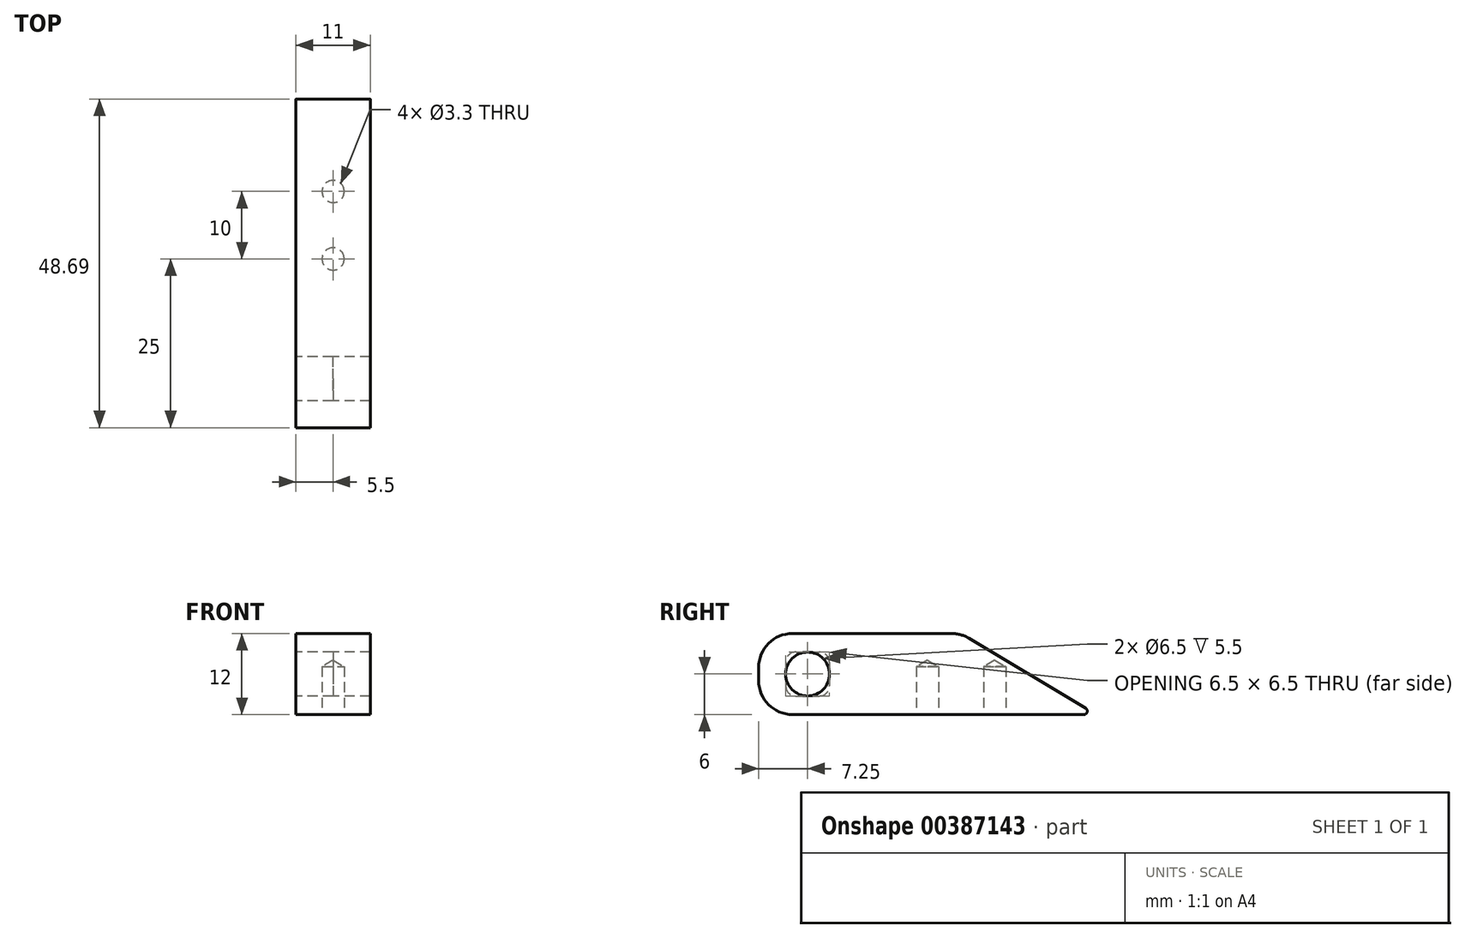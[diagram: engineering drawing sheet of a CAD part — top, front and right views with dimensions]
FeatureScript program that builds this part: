
annotation { "Feature Type Name" : "Feature", "Feature Type Description" : "" }
export const myFeature = defineFeature(function(context is Context, id is Id, definition is map)
    precondition{}
    {
        {
            var Q0;
            Q0=qCreatedBy(makeId("Front.planeOp"),FACE);
            var sketch = newSketch(context, id + "F0", { "sketchPlane" : qUnion([Q0])});
            skLineSegment(sketch, "E0.bottom", {"start": v(5.5, 6) * mm, "end": v(-5.5, 6) * mm});
            skLineSegment(sketch, "E0.top", {"start": v(5.5, -6) * mm, "end": v(-5.5, -6) * mm});
            skLineSegment(sketch, "E0.left", {"start": v(5.5, 6) * mm, "end": v(5.5, -6) * mm});
            skLineSegment(sketch, "E0.right", {"start": v(-5.5, 6) * mm, "end": v(-5.5, -6) * mm});
            skPoint(sketch, "E0.middle", {"position": v(0, 0) * mm});
            skSolve(sketch);
        }
        {
            var Q0;
            Q0 = qSketchRegion(id + "F0", true);
            extrude(context, id + "F1", {"entities" : qUnion([Q0]), "endBound" : BoundingType.SYMMETRIC, "depth" : 50 * mm});
        }
        {
            var Q0;
            Q0=makeQuery(id+"F1.opExtrude","SWEPT_FACE",FACE,{"disambiguationData":[OSD([sQuery(id+"F0.wireOp",EDGE,"E0.right")])]});
            var sketch = newSketch(context, id + "F2", { "sketchPlane" : qUnion([Q0])});
            skLineSegment(sketch, "E1.bottom", {"start": v(21, 3.25) * mm, "end": v(14.5, 3.25) * mm});
            skLineSegment(sketch, "E1.top", {"start": v(21, -3.25) * mm, "end": v(14.5, -3.25) * mm});
            skLineSegment(sketch, "E1.left", {"start": v(21, 3.25) * mm, "end": v(21, -3.25) * mm});
            skLineSegment(sketch, "E1.right", {"start": v(14.5, 3.25) * mm, "end": v(14.5, -3.25) * mm});
            skPoint(sketch, "E2.centerSnap0", {"position": v(21, 0) * mm});
            skPoint(sketch, "E2.centerSnap1", {"position": v(17.75, 3.25) * mm});
            skSolve(sketch);
        }
        {
            var Q0;
            Q0 = qSketchRegion(id + "F2", true);
            extrude(context, id + "F3", {"entities" : qUnion([Q0]), "operationType" : NewBodyOperationType.REMOVE, "oppositeDirection" : true, "depth" : 5.5 * mm});
        }
        {
            var Q0;
            Q0=makeQuery(id+"F3.boolean.opBoolean","COPY",FACE,{"derivedFrom":makeQuery(id+"F3.opExtrude","CAP_FACE",FACE,{"disambiguationData":[OSD([sQuery(id+"F2.wireOp",EDGE,"E1.bottom"),sQuery(id+"F2.wireOp",EDGE,"E1.top"),sQuery(id+"F2.wireOp",EDGE,"E1.left"),sQuery(id+"F2.wireOp",EDGE,"E1.right")])],"isStart":false})});
            var sketch = newSketch(context, id + "F4", { "sketchPlane" : qUnion([Q0])});
            skCircle(sketch, "E3", {"center": v(17.75, 0) * mm, "radius": 3.25 * mm});
            skPoint(sketch, "E3.centerSnap0", {"position": v(21, 0) * mm});
            skPoint(sketch, "E3.centerSnap1", {"position": v(17.75, 3.25) * mm});
            skSolve(sketch);
        }
        {
            var Q0;
            Q0 = qSketchRegion(id + "F4", true);
            extrude(context, id + "F5", {"entities" : qUnion([Q0]), "operationType" : NewBodyOperationType.REMOVE, "oppositeDirection" : true, "depth" : 25 * mm});
        }
        {
            var Q0;
            Q0=makeQuery(id+"F3.boolean.opBoolean","COPY",EDGE,{"derivedFrom":makeQuery(id+"F3.opExtrude","SWEPT_EDGE",EDGE,{"disambiguationData":[OSD([sQuery(id+"F2.wireOp",EDGE,"E1.bottom"),sQuery(id+"F2.wireOp",EDGE,"E1.right")])]})});
            var Q1;
            Q1=makeQuery(id+"F3.boolean.opBoolean","COPY",EDGE,{"derivedFrom":makeQuery(id+"F3.opExtrude","SWEPT_EDGE",EDGE,{"disambiguationData":[OSD([sQuery(id+"F2.wireOp",EDGE,"E1.bottom"),sQuery(id+"F2.wireOp",EDGE,"E1.left")])]})});
            var Q2;
            Q2=makeQuery(id+"F3.boolean.opBoolean","COPY",EDGE,{"derivedFrom":makeQuery(id+"F3.opExtrude","SWEPT_EDGE",EDGE,{"disambiguationData":[OSD([sQuery(id+"F2.wireOp",EDGE,"E1.top"),sQuery(id+"F2.wireOp",EDGE,"E1.left")])]})});
            var Q3;
            Q3=makeQuery(id+"F3.boolean.opBoolean","COPY",EDGE,{"derivedFrom":makeQuery(id+"F3.opExtrude","SWEPT_EDGE",EDGE,{"disambiguationData":[OSD([sQuery(id+"F2.wireOp",EDGE,"E1.top"),sQuery(id+"F2.wireOp",EDGE,"E1.right")])]})});
            fillet(context, id + "F6", {"entities" : qUnion([Q0, Q1, Q2, Q3]), "radius" : 1.5 * mm, "tangentPropagation" : true, "allowEdgeOverflow" : false});
        }
        {
            var Q0;
            Q0=makeQuery(id+"F1.opExtrude","CAP_EDGE",EDGE,{"disambiguationData":[OSD([sQuery(id+"F0.wireOp",EDGE,"E0.bottom")])],"isStart":true});
            chamfer(context, id + "F7", {"entities" : qUnion([Q0]), "chamferType" : ChamferType.TWO_OFFSETS, "width1" : 20 * mm, "oppositeDirection" : false, "width2" : 12 * mm, "tangentPropagation" : true});
        }
        {
            var Q0;
            Q0=makeQuery(id+"F1.opExtrude","SWEPT_FACE",FACE,{"disambiguationData":[OSD([sQuery(id+"F0.wireOp",EDGE,"E0.top")])]});
            var sketch = newSketch(context, id + "F8", { "sketchPlane" : qUnion([Q0])});
            skLineSegment(sketch, "E4", {"start": v(0, 25) * mm, "end": v(0, 0) * mm});
            skLineSegment(sketch, "E5", {"start": v(0, 0) * mm, "end": v(0, -10) * mm});
            skSolve(sketch);
        }
        {
            var Q0;
            Q0=sQuery(id+"F8.wireOp",VERTEX,"E4.end");
            var Q1;
            Q1=sQuery(id+"F8.wireOp",VERTEX,"E5.end");
            var Q2;
            Q2=makeQuery(id+"F1.opExtrude","SWEPT_BODY",BODY,{"disambiguationData":[OSD([sQuery(id+"F0.wireOp",EDGE,"E0.bottom"),sQuery(id+"F0.wireOp",EDGE,"E0.top"),sQuery(id+"F0.wireOp",EDGE,"E0.left"),sQuery(id+"F0.wireOp",EDGE,"E0.right")])]});
            hole(context, id + "F9", {"style" : HoleStyle.SIMPLE, "endStyle" : HoleEndStyle.BLIND, "standardTappedOrClearance" : lookupTablePath({ "standard" : "ISO", "engagement" : "75%", "pitch" : "0.7 mm", "size" : "M4", "type" : "Tapped" }), "standardBlindInLast" : lookupTablePath({ "standard" : "ISO", "engagement" : "75%", "pitch" : "0.7 mm", "size" : "M4", "type" : "Tapped" }), "holeDiameter" : 3.3 * mm, "showTappedDepth" : true, "holeDepth" : 7.1 * mm, "isTappedThrough" : true, "tappedDepth" : 5 * mm, "tapClearance" : 3, "startFromSketch" : true, "locations" : qUnion([Q0, Q1]), "scope" : qUnion([Q2]), "majorDiameter" : 4 * mm});
        }
        {
            var Q0;
            {var subQ0=sQuery(id+"F0.wireOp",EDGE,"E0.bottom");Q0=makeQuery(id+"F7.opChamfer","BLEND_EDGE",EDGE,{"blendedFrom":[makeQuery(id+"F1.opExtrude","CAP_EDGE",EDGE,{"disambiguationData":[OSD([subQ0])],"isStart":true}),makeQuery(id+"F1.opExtrude","SWEPT_FACE",FACE,{"disambiguationData":[OSD([subQ0])]})],"blendedInto":[makeQuery(id+"F1.opExtrude","SWEPT_FACE",FACE,{"disambiguationData":[OSD([subQ0])]})]});}
            var Q1;
            Q1=makeQuery(id+"F1.opExtrude","CAP_EDGE",EDGE,{"disambiguationData":[OSD([sQuery(id+"F0.wireOp",EDGE,"E0.bottom")])],"isStart":false});
            var Q2;
            Q2=makeQuery(id+"F1.opExtrude","CAP_EDGE",EDGE,{"disambiguationData":[OSD([sQuery(id+"F0.wireOp",EDGE,"E0.top")])],"isStart":false});
            fillet(context, id + "F10", {"entities" : qUnion([Q0, Q1, Q2]), "radius" : 5 * mm, "tangentPropagation" : true, "allowEdgeOverflow" : false});
        }
        {
            var Q0;
            Q0=makeQuery(id+"F7.opChamfer","BLEND_EDGE",EDGE,{"blendedFrom":[makeQuery(id+"F1.opExtrude","CAP_EDGE",EDGE,{"disambiguationData":[OSD([sQuery(id+"F0.wireOp",EDGE,"E0.bottom")])],"isStart":true}),makeQuery(id+"F1.opExtrude","SWEPT_FACE",FACE,{"disambiguationData":[OSD([sQuery(id+"F0.wireOp",EDGE,"E0.top")])]})],"blendedInto":[makeQuery(id+"F1.opExtrude","SWEPT_FACE",FACE,{"disambiguationData":[OSD([sQuery(id+"F0.wireOp",EDGE,"E0.top")])]})]});
            fillet(context, id + "F11", {"entities" : qUnion([Q0]), "radius" : .5 * mm, "tangentPropagation" : true, "allowEdgeOverflow" : false});
        }
    });
